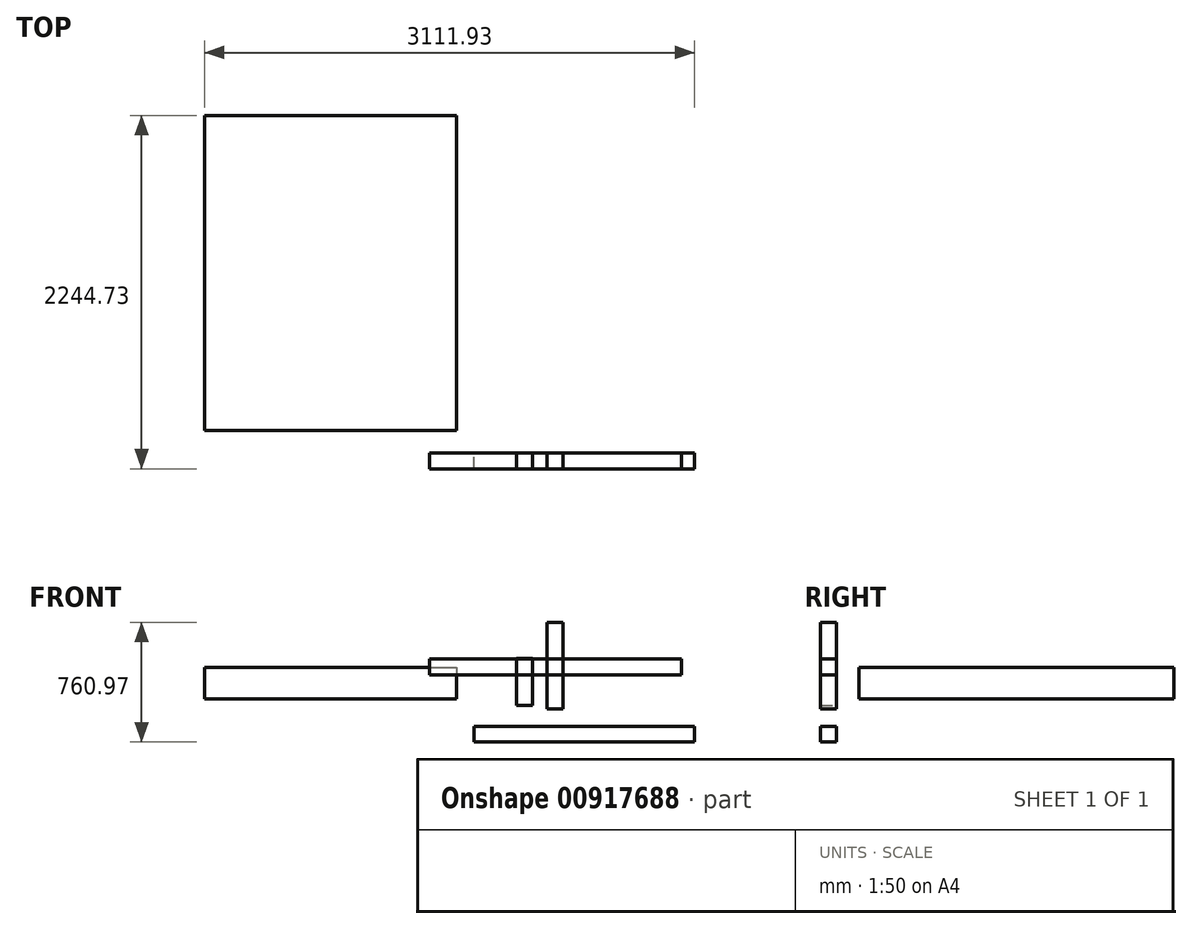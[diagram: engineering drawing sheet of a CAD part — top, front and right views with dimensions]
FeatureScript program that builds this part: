
annotation { "Feature Type Name" : "Feature", "Feature Type Description" : "" }
export const myFeature = defineFeature(function(context is Context, id is Id, definition is map)
    precondition{}
    {
        {
            var Q0;
            Q0=qCreatedBy(makeId("Front.planeOp"),FACE);
            var sketch = newSketch(context, id + "F0", { "sketchPlane" : qUnion([Q0])});
            skLineSegment(sketch, "E0.bottom", {"start": v(-451.99, 258.72) * mm, "end": v(-351.99, 258.72) * mm});
            skLineSegment(sketch, "E0.top", {"start": v(-451.99, -41.28) * mm, "end": v(-351.99, -41.28) * mm});
            skLineSegment(sketch, "E0.left", {"start": v(-451.99, 258.72) * mm, "end": v(-451.99, -41.28) * mm});
            skLineSegment(sketch, "E0.right", {"start": v(-351.99, 258.72) * mm, "end": v(-351.99, -41.28) * mm});
            skSolve(sketch);
        }
        {
            var Q0;
            Q0 = qSketchRegion(id + "F0", true);
            extrude(context, id + "F1", {"entities" : qUnion([Q0]), "depth" : 100 * mm, "offsetDistance" : 25 * mm});
        }
        {
            var Q0;
            Q0=qCreatedBy(makeId("Front.planeOp"),FACE);
            var sketch = newSketch(context, id + "F2", { "sketchPlane" : qUnion([Q0])});
            skLineSegment(sketch, "E1.bottom", {"start": v(-258.13, 486.64) * mm, "end": v(-158.13, 486.64) * mm});
            skLineSegment(sketch, "E1.top", {"start": v(-258.13, -63.36) * mm, "end": v(-158.13, -63.36) * mm});
            skLineSegment(sketch, "E1.left", {"start": v(-258.13, 486.64) * mm, "end": v(-258.13, -63.36) * mm});
            skLineSegment(sketch, "E1.right", {"start": v(-158.13, 486.64) * mm, "end": v(-158.13, -63.36) * mm});
            skSolve(sketch);
        }
        {
            var Q0;
            Q0 = qSketchRegion(id + "F2", true);
            extrude(context, id + "F3", {"entities" : qUnion([Q0]), "depth" : 100 * mm, "offsetDistance" : 25 * mm});
        }
        {
            var Q0;
            Q0=qCreatedBy(makeId("Front.planeOp"),FACE);
            var sketch = newSketch(context, id + "F4", { "sketchPlane" : qUnion([Q0])});
            skLineSegment(sketch, "E2.bottom", {"start": v(-1005.11, 252.5) * mm, "end": v(594.89, 252.5) * mm});
            skLineSegment(sketch, "E2.top", {"start": v(-1005.11, 152.5) * mm, "end": v(594.89, 152.5) * mm});
            skLineSegment(sketch, "E2.left", {"start": v(-1005.11, 252.5) * mm, "end": v(-1005.11, 152.5) * mm});
            skLineSegment(sketch, "E2.right", {"start": v(594.89, 252.5) * mm, "end": v(594.89, 152.5) * mm});
            skSolve(sketch);
        }
        {
            var Q0;
            Q0 = qSketchRegion(id + "F4", true);
            extrude(context, id + "F5", {"entities" : qUnion([Q0]), "depth" : 100 * mm, "offsetDistance" : 25 * mm});
        }
        {
            var Q0;
            Q0=qCreatedBy(makeId("Front.planeOp"),FACE);
            var sketch = newSketch(context, id + "F6", { "sketchPlane" : qUnion([Q0])});
            skLineSegment(sketch, "E3.bottom", {"start": v(-721.12, -174.33) * mm, "end": v(678.88, -174.33) * mm});
            skLineSegment(sketch, "E3.top", {"start": v(-721.12, -274.33) * mm, "end": v(678.88, -274.33) * mm});
            skLineSegment(sketch, "E3.left", {"start": v(-721.12, -174.33) * mm, "end": v(-721.12, -274.33) * mm});
            skLineSegment(sketch, "E3.right", {"start": v(678.88, -174.33) * mm, "end": v(678.88, -274.33) * mm});
            skSolve(sketch);
        }
        {
            var Q0;
            Q0 = qSketchRegion(id + "F6", true);
            extrude(context, id + "F7", {"entities" : qUnion([Q0]), "depth" : 100 * mm, "offsetDistance" : 25 * mm});
        }
        {
            var Q0;
            Q0=qCreatedBy(makeId("Top.planeOp"),FACE);
            var sketch = newSketch(context, id + "F8", { "sketchPlane" : qUnion([Q0])});
            skLineSegment(sketch, "E4.bottom", {"start": v(-2433.05, 2144.73) * mm, "end": v(-833.05, 2144.73) * mm});
            skLineSegment(sketch, "E4.top", {"start": v(-2433.05, 144.73) * mm, "end": v(-833.05, 144.73) * mm});
            skLineSegment(sketch, "E4.left", {"start": v(-2433.05, 2144.73) * mm, "end": v(-2433.05, 144.73) * mm});
            skLineSegment(sketch, "E4.right", {"start": v(-833.05, 2144.73) * mm, "end": v(-833.05, 144.73) * mm});
            skSolve(sketch);
        }
        {
            var Q0;
            Q0 = qSketchRegion(id + "F8", true);
            extrude(context, id + "F9", {"entities" : qUnion([Q0]), "depth" : 200 * mm, "offsetDistance" : 25 * mm});
        }
    });
